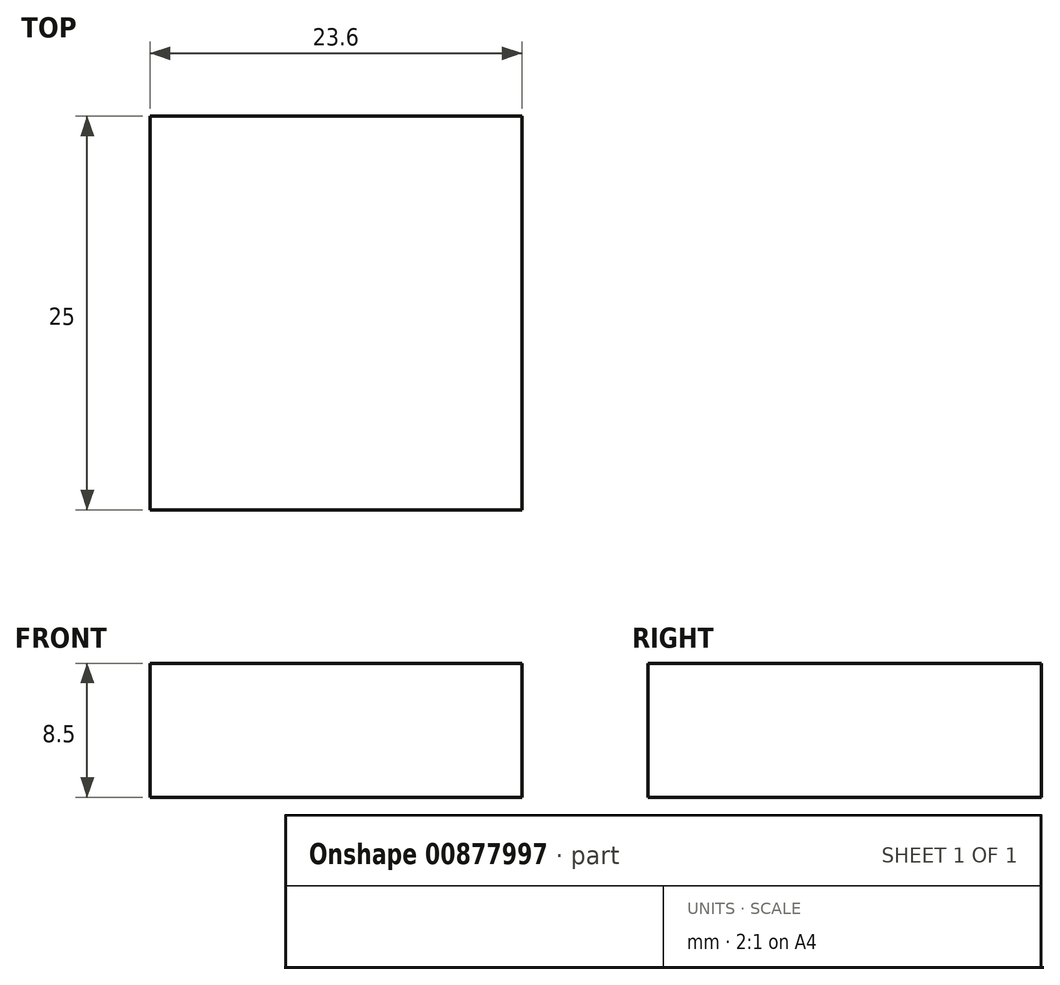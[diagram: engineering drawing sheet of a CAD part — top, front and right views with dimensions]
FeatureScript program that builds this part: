
annotation { "Feature Type Name" : "Feature", "Feature Type Description" : "" }
export const myFeature = defineFeature(function(context is Context, id is Id, definition is map)
    precondition{}
    {
        {
            var Q0;
            Q0=qCreatedBy(makeId("Front.planeOp"),FACE);
            var sketch = newSketch(context, id + "F0", { "sketchPlane" : qUnion([Q0])});
            skLineSegment(sketch, "E0.bottom", {"start": v(-11.8, 4.25) * mm, "end": v(11.8, 4.25) * mm});
            skLineSegment(sketch, "E0.top", {"start": v(-11.8, -4.25) * mm, "end": v(11.8, -4.25) * mm});
            skLineSegment(sketch, "E0.left", {"start": v(-11.8, 4.25) * mm, "end": v(-11.8, -4.25) * mm});
            skLineSegment(sketch, "E0.right", {"start": v(11.8, 4.25) * mm, "end": v(11.8, -4.25) * mm});
            skSolve(sketch);
        }
        {
            var Q0;
            Q0=makeQuery(id+"F0.imprint","IMPRINT",FACE,{"disambiguationData":[TD([[makeQuery(id+"F0.imprint","IMPRINT",EDGE,{"derivedFrom":sQuery(id+"F0.wireOp",EDGE,"E0.bottom")}),-1.0]])]});
            extrude(context, id + "F1", {"entities" : qUnion([Q0]), "depth" : 25 * mm, "offsetDistance" : 25 * mm});
        }
    });
